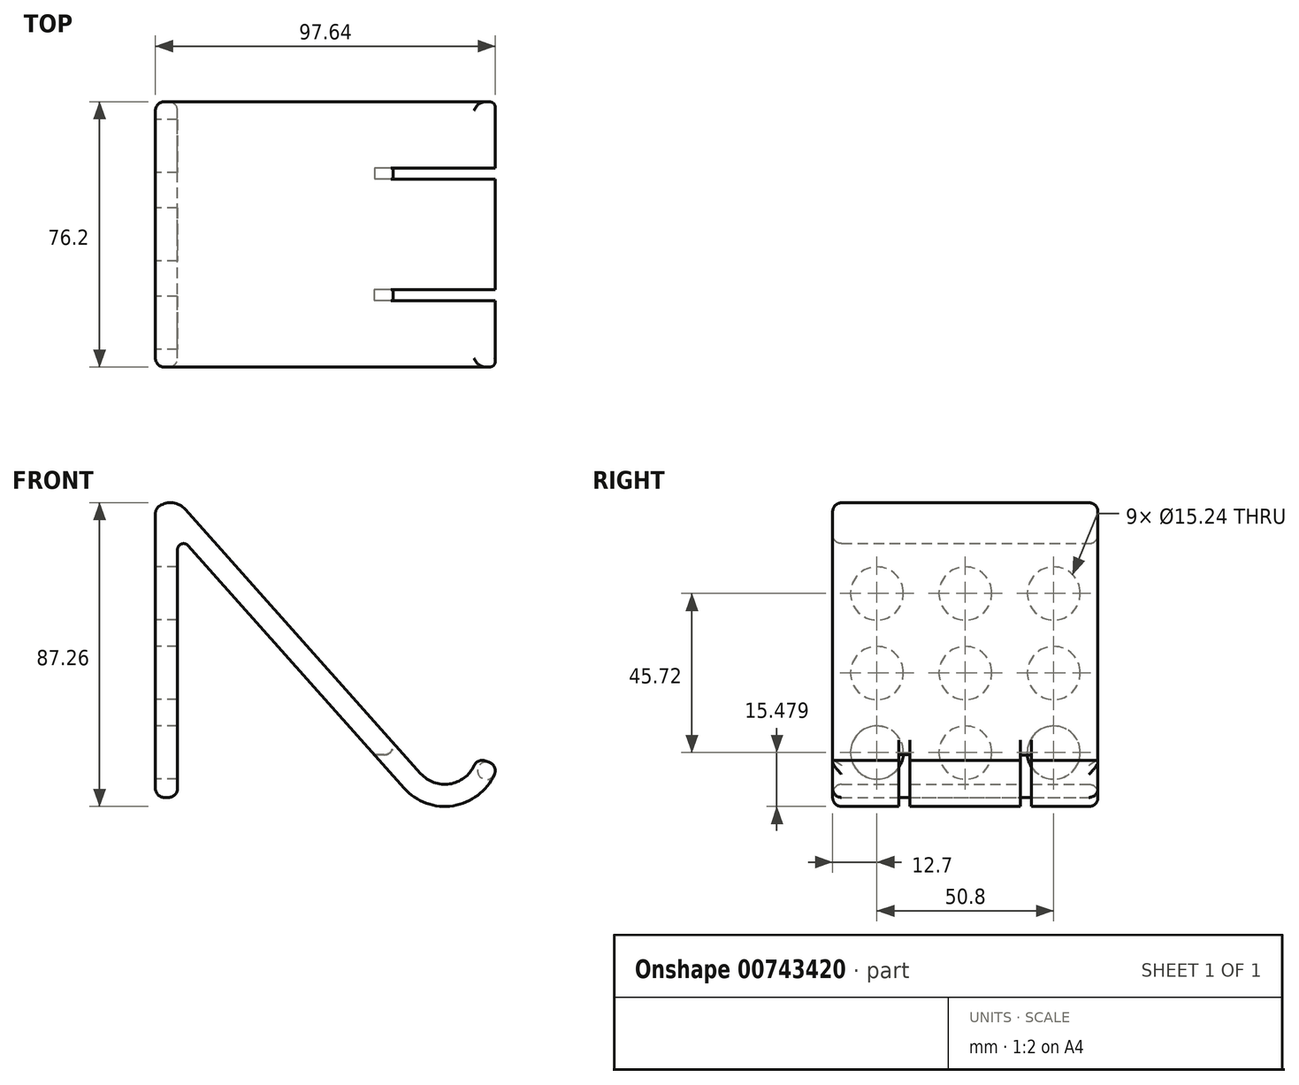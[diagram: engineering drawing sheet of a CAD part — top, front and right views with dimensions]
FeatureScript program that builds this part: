
annotation { "Feature Type Name" : "Feature", "Feature Type Description" : "" }
export const myFeature = defineFeature(function(context is Context, id is Id, definition is map)
    precondition{}
    {
        {
            var Q0;
            Q0=qCreatedBy(makeId("Front.planeOp"),FACE);
            var sketch = newSketch(context, id + "F0", { "sketchPlane" : qUnion([Q0])});
            skLineSegment(sketch, "E0", {"start": v(-38.8, 49.32) * mm, "end": v(28.78, -26.54) * mm});
            skArc(sketch, "E1", {"start": v(28.78, -26.54) * mm, "mid": v(38.21, -29.3) * mm, "end": v(44.82, -22.03) * mm});
            skArc(sketch, "E2", {"start": v(-38.8, 49.32) * mm, "mid": v(-43.13, 51.27) * mm, "end": v(-47.46, 49.32) * mm});
            skLineSegment(sketch, "E3", {"start": v(-47.46, 49.32) * mm, "end": v(-47.46, -33.4) * mm});
            skLineSegment(sketch, "E4", {"start": v(-47.46, -33.4) * mm, "end": v(-41.1, -33.4) * mm});
            skLineSegment(sketch, "E5", {"start": v(-41.1, -33.4) * mm, "end": v(-41.1, 37.8) * mm});
            skLineSegment(sketch, "E6", {"start": v(-38.07, 38.96) * mm, "end": v(24.04, -30.76) * mm});
            skArc(sketch, "E7", {"start": v(24.04, -30.76) * mm, "mid": v(39.43, -35.54) * mm, "end": v(50.85, -24.18) * mm});
            skLineSegment(sketch, "E8", {"start": v(50.85, -24.18) * mm, "end": v(44.82, -22.03) * mm});
            skArc(sketch, "E9", {"start": v(-38.07, 38.96) * mm, "mid": v(-39.99, 39.42) * mm, "end": v(-41.1, 37.8) * mm});
            skSolve(sketch);
        }
        {
            var Q0;
            Q0 = qSketchRegion(id + "F0", true);
            extrude(context, id + "F1", {"entities" : qUnion([Q0]), "depth" : 76.2 * mm, "offsetDistance" : 25.4 * mm});
        }
        {
            var Q0;
            Q0=makeQuery(id+"F1.opExtrude","SWEPT_FACE",FACE,{"disambiguationData":[OSD([sQuery(id+"F0.wireOp",EDGE,"E3")])]});
            var sketch = newSketch(context, id + "F2", { "sketchPlane" : qUnion([Q0])});
            skCircle(sketch, "E10", {"center": v(12.7, -20.51) * mm, "radius": 7.62 * mm});
            skCircle(sketch, "E11.1.0.0", {"center": v(38.1, -20.51) * mm, "radius": 7.62 * mm});
            skCircle(sketch, "E11.2.0.0", {"center": v(63.5, -20.51) * mm, "radius": 7.62 * mm});
            skLineSegment(sketch, "E11.direction1", {"start": v(12.7, -20.51) * mm, "end": v(38.1, -20.51) * mm, "construction": true});
            skCircle(sketch, "E12.1.0.0", {"center": v(12.7, 2.35) * mm, "radius": 7.62 * mm});
            skCircle(sketch, "E12.1.0.1", {"center": v(38.1, 2.35) * mm, "radius": 7.62 * mm});
            skCircle(sketch, "E12.1.0.2", {"center": v(63.5, 2.35) * mm, "radius": 7.62 * mm});
            skCircle(sketch, "E12.2.0.0", {"center": v(12.7, 25.2) * mm, "radius": 7.62 * mm});
            skCircle(sketch, "E12.2.0.1", {"center": v(38.1, 25.2) * mm, "radius": 7.62 * mm});
            skCircle(sketch, "E12.2.0.2", {"center": v(63.5, 25.2) * mm, "radius": 7.62 * mm});
            skLineSegment(sketch, "E12.direction1", {"start": v(12.7, -20.51) * mm, "end": v(12.7, 2.35) * mm, "construction": true});
            skSolve(sketch);
        }
        {
            var Q0;
            Q0 = qSketchRegion(id + "F2", true);
            extrude(context, id + "F3", {"entities" : qUnion([Q0]), "operationType" : NewBodyOperationType.REMOVE, "oppositeDirection" : true, "depth" : 6.35 * mm, "offsetDistance" : 25.4 * mm});
        }
        {
            var Q0;
            Q0=qCreatedBy(makeId("Right.planeOp"),FACE);
            var sketch = newSketch(context, id + "F4", { "sketchPlane" : qUnion([Q0])});
            skLineSegment(sketch, "E13.bottom", {"start": v(-57.15, -21.1) * mm, "end": v(-53.98, -21.1) * mm});
            skLineSegment(sketch, "E13.top", {"start": v(-57.15, -36.34) * mm, "end": v(-53.98, -36.34) * mm});
            skLineSegment(sketch, "E13.left", {"start": v(-57.15, -21.1) * mm, "end": v(-57.15, -36.34) * mm});
            skLineSegment(sketch, "E13.right", {"start": v(-53.98, -21.1) * mm, "end": v(-53.98, -36.34) * mm});
            skLineSegment(sketch, "E14.bottom", {"start": v(-22.23, -21.18) * mm, "end": v(-19.05, -21.18) * mm});
            skLineSegment(sketch, "E14.top", {"start": v(-22.23, -36.42) * mm, "end": v(-19.05, -36.42) * mm});
            skLineSegment(sketch, "E14.left", {"start": v(-22.23, -21.18) * mm, "end": v(-22.23, -36.42) * mm});
            skLineSegment(sketch, "E14.right", {"start": v(-19.05, -21.18) * mm, "end": v(-19.05, -36.42) * mm});
            skSolve(sketch);
        }
        {
            var Q0;
            Q0 = qSketchRegion(id + "F4", true);
            extrude(context, id + "F5", {"entities" : qUnion([Q0]), "operationType" : NewBodyOperationType.REMOVE, "depth" : 76.2 * mm, "offsetDistance" : 25.4 * mm});
        }
        {
            var Q0;
            Q0=makeQuery(id+"F1.opExtrude","SWEPT_EDGE",EDGE,{"disambiguationData":[OSD([sQuery(id+"F0.wireOp",EDGE,"E4"),sQuery(id+"F0.wireOp",EDGE,"E5")])]});
            var Q1;
            Q1=makeQuery(id+"F1.opExtrude","SWEPT_EDGE",EDGE,{"disambiguationData":[OSD([sQuery(id+"F0.wireOp",EDGE,"E3"),sQuery(id+"F0.wireOp",EDGE,"E4")])]});
            var Q2;
            Q2=makeQuery(id+"F1.opExtrude","CAP_EDGE",EDGE,{"disambiguationData":[OSD([sQuery(id+"F0.wireOp",EDGE,"E4")])],"isStart":true});
            var Q3;
            Q3=makeQuery(id+"F1.opExtrude","CAP_EDGE",EDGE,{"disambiguationData":[OSD([sQuery(id+"F0.wireOp",EDGE,"E4")])],"isStart":false});
            var Q4;
            Q4=makeQuery(id+"F1.opExtrude","CAP_EDGE",EDGE,{"disambiguationData":[OSD([sQuery(id+"F0.wireOp",EDGE,"E5")])],"isStart":true});
            var Q5;
            Q5=makeQuery(id+"F1.opExtrude","CAP_EDGE",EDGE,{"disambiguationData":[OSD([sQuery(id+"F0.wireOp",EDGE,"E3")])],"isStart":true});
            var Q6;
            Q6=makeQuery(id+"F1.opExtrude","SWEPT_EDGE",EDGE,{"disambiguationData":[OSD([sQuery(id+"F0.wireOp",EDGE,"E2"),sQuery(id+"F0.wireOp",EDGE,"E3")])]});
            var Q7;
            Q7=makeQuery(id+"F1.opExtrude","CAP_EDGE",EDGE,{"disambiguationData":[OSD([sQuery(id+"F0.wireOp",EDGE,"E3")])],"isStart":false});
            var Q8;
            Q8=makeQuery(id+"F1.opExtrude","CAP_EDGE",EDGE,{"disambiguationData":[OSD([sQuery(id+"F0.wireOp",EDGE,"E5")])],"isStart":false});
            var Q9;
            Q9=makeQuery(id+"F1.opExtrude","CAP_EDGE",EDGE,{"disambiguationData":[OSD([sQuery(id+"F0.wireOp",EDGE,"E2")])],"isStart":true});
            var Q10;
            Q10=makeQuery(id+"F1.opExtrude","CAP_EDGE",EDGE,{"disambiguationData":[OSD([sQuery(id+"F0.wireOp",EDGE,"E0")])],"isStart":true});
            var Q11;
            Q11=makeQuery(id+"F1.opExtrude","CAP_EDGE",EDGE,{"disambiguationData":[OSD([sQuery(id+"F0.wireOp",EDGE,"E2")])],"isStart":false});
            var Q12;
            {var subQ0=sQuery(id+"F0.wireOp",EDGE,"E7");var subQ1=sQuery(id+"F0.wireOp",EDGE,"E8");Q12=makeQuery(id+"F5.boolean.opBoolean","SPLIT",EDGE,{"disambiguationData":[TD([makeQuery(id+"F5.opExtrude","SWEPT_FACE",FACE,{"disambiguationData":[OSD([sQuery(id+"F4.wireOp",EDGE,"E13.right")])]})])],"derivedFrom":makeQuery(id+"F1.opExtrude","SWEPT_EDGE",EDGE,{"disambiguationData":[OSD([subQ0,subQ1])]})});}
            var Q13;
            {var subQ0=sQuery(id+"F0.wireOp",EDGE,"E1");var subQ1=sQuery(id+"F0.wireOp",EDGE,"E8");Q13=makeQuery(id+"F5.boolean.opBoolean","SPLIT",EDGE,{"disambiguationData":[TD([makeQuery(id+"F5.opExtrude","SWEPT_FACE",FACE,{"disambiguationData":[OSD([sQuery(id+"F4.wireOp",EDGE,"E13.right")])]})])],"derivedFrom":makeQuery(id+"F1.opExtrude","SWEPT_EDGE",EDGE,{"disambiguationData":[OSD([subQ0,subQ1])]})});}
            var Q14;
            {var subQ0=sQuery(id+"F0.wireOp",EDGE,"E8");var subQ1=sQuery(id+"F0.wireOp",EDGE,"E7");Q14=makeQuery(id+"F5.boolean.opBoolean","SPLIT",EDGE,{"disambiguationData":[TD([makeQuery(id+"F5.opExtrude","SWEPT_FACE",FACE,{"disambiguationData":[OSD([sQuery(id+"F4.wireOp",EDGE,"E14.right")])]})])],"derivedFrom":makeQuery(id+"F1.opExtrude","SWEPT_EDGE",EDGE,{"disambiguationData":[OSD([subQ1,subQ0])]})});}
            var Q15;
            {var subQ0=sQuery(id+"F0.wireOp",EDGE,"E8");var subQ1=sQuery(id+"F0.wireOp",EDGE,"E1");Q15=makeQuery(id+"F5.boolean.opBoolean","SPLIT",EDGE,{"disambiguationData":[TD([makeQuery(id+"F5.opExtrude","SWEPT_FACE",FACE,{"disambiguationData":[OSD([sQuery(id+"F4.wireOp",EDGE,"E14.right")])]})])],"derivedFrom":makeQuery(id+"F1.opExtrude","SWEPT_EDGE",EDGE,{"disambiguationData":[OSD([subQ1,subQ0])]})});}
            var Q16;
            {var subQ0=sQuery(id+"F0.wireOp",EDGE,"E8");var subQ1=sQuery(id+"F0.wireOp",EDGE,"E7");Q16=makeQuery(id+"F5.boolean.opBoolean","SPLIT",EDGE,{"disambiguationData":[TD([makeQuery(id+"F5.opExtrude","SWEPT_FACE",FACE,{"disambiguationData":[OSD([sQuery(id+"F4.wireOp",EDGE,"E13.left")])]})])],"derivedFrom":makeQuery(id+"F1.opExtrude","SWEPT_EDGE",EDGE,{"disambiguationData":[OSD([subQ1,subQ0])]})});}
            var Q17;
            {var subQ0=sQuery(id+"F0.wireOp",EDGE,"E8");var subQ1=sQuery(id+"F0.wireOp",EDGE,"E1");Q17=makeQuery(id+"F5.boolean.opBoolean","SPLIT",EDGE,{"disambiguationData":[TD([makeQuery(id+"F5.opExtrude","SWEPT_FACE",FACE,{"disambiguationData":[OSD([sQuery(id+"F4.wireOp",EDGE,"E13.left")])]})])],"derivedFrom":makeQuery(id+"F1.opExtrude","SWEPT_EDGE",EDGE,{"disambiguationData":[OSD([subQ1,subQ0])]})});}
            var Q18;
            Q18=makeQuery(id+"F3.boolean.opBoolean","COPY",EDGE,{"derivedFrom":makeQuery(id+"F3.opExtrude","CAP_EDGE",EDGE,{"disambiguationData":[OSD([sQuery(id+"F2.wireOp",EDGE,"E12.1.0.0")])],"isStart":false})});
            var Q19;
            Q19=makeQuery(id+"F3.boolean.opBoolean","COPY",EDGE,{"derivedFrom":makeQuery(id+"F3.opExtrude","CAP_EDGE",EDGE,{"disambiguationData":[OSD([sQuery(id+"F2.wireOp",EDGE,"E12.2.0.0")])],"isStart":false})});
            var Q20;
            Q20=makeQuery(id+"F3.boolean.opBoolean","COPY",EDGE,{"derivedFrom":makeQuery(id+"F3.opExtrude","CAP_EDGE",EDGE,{"disambiguationData":[OSD([sQuery(id+"F2.wireOp",EDGE,"E10")])],"isStart":false})});
            var Q21;
            Q21=makeQuery(id+"F3.boolean.opBoolean","COPY",EDGE,{"derivedFrom":makeQuery(id+"F3.opExtrude","CAP_EDGE",EDGE,{"disambiguationData":[OSD([sQuery(id+"F2.wireOp",EDGE,"E11.1.0.0")])],"isStart":false})});
            var Q22;
            Q22=makeQuery(id+"F3.boolean.opBoolean","COPY",EDGE,{"derivedFrom":makeQuery(id+"F3.opExtrude","CAP_EDGE",EDGE,{"disambiguationData":[OSD([sQuery(id+"F2.wireOp",EDGE,"E12.1.0.1")])],"isStart":false})});
            var Q23;
            Q23=makeQuery(id+"F3.boolean.opBoolean","COPY",EDGE,{"derivedFrom":makeQuery(id+"F3.opExtrude","CAP_EDGE",EDGE,{"disambiguationData":[OSD([sQuery(id+"F2.wireOp",EDGE,"E12.2.0.1")])],"isStart":false})});
            var Q24;
            Q24=makeQuery(id+"F3.boolean.opBoolean","COPY",EDGE,{"derivedFrom":makeQuery(id+"F3.opExtrude","CAP_EDGE",EDGE,{"disambiguationData":[OSD([sQuery(id+"F2.wireOp",EDGE,"E11.2.0.0")])],"isStart":false})});
            var Q25;
            Q25=makeQuery(id+"F3.boolean.opBoolean","COPY",EDGE,{"derivedFrom":makeQuery(id+"F3.opExtrude","CAP_EDGE",EDGE,{"disambiguationData":[OSD([sQuery(id+"F2.wireOp",EDGE,"E12.1.0.2")])],"isStart":false})});
            var Q26;
            Q26=makeQuery(id+"F3.boolean.opBoolean","COPY",EDGE,{"derivedFrom":makeQuery(id+"F3.opExtrude","CAP_EDGE",EDGE,{"disambiguationData":[OSD([sQuery(id+"F2.wireOp",EDGE,"E12.2.0.2")])],"isStart":false})});
            var Q27;
            Q27=makeQuery(id+"F3.boolean.opBoolean","COPY",EDGE,{"derivedFrom":makeQuery(id+"F3.opExtrude","CAP_EDGE",EDGE,{"disambiguationData":[OSD([sQuery(id+"F2.wireOp",EDGE,"E12.2.0.0")])],"isStart":true})});
            var Q28;
            Q28=makeQuery(id+"F3.boolean.opBoolean","COPY",EDGE,{"derivedFrom":makeQuery(id+"F3.opExtrude","CAP_EDGE",EDGE,{"disambiguationData":[OSD([sQuery(id+"F2.wireOp",EDGE,"E12.2.0.1")])],"isStart":true})});
            var Q29;
            Q29=makeQuery(id+"F3.boolean.opBoolean","COPY",EDGE,{"derivedFrom":makeQuery(id+"F3.opExtrude","CAP_EDGE",EDGE,{"disambiguationData":[OSD([sQuery(id+"F2.wireOp",EDGE,"E12.2.0.2")])],"isStart":true})});
            var Q30;
            Q30=makeQuery(id+"F3.boolean.opBoolean","COPY",EDGE,{"derivedFrom":makeQuery(id+"F3.opExtrude","CAP_EDGE",EDGE,{"disambiguationData":[OSD([sQuery(id+"F2.wireOp",EDGE,"E12.1.0.2")])],"isStart":true})});
            var Q31;
            Q31=makeQuery(id+"F3.boolean.opBoolean","COPY",EDGE,{"derivedFrom":makeQuery(id+"F3.opExtrude","CAP_EDGE",EDGE,{"disambiguationData":[OSD([sQuery(id+"F2.wireOp",EDGE,"E12.1.0.1")])],"isStart":true})});
            var Q32;
            Q32=makeQuery(id+"F3.boolean.opBoolean","COPY",EDGE,{"derivedFrom":makeQuery(id+"F3.opExtrude","CAP_EDGE",EDGE,{"disambiguationData":[OSD([sQuery(id+"F2.wireOp",EDGE,"E12.1.0.0")])],"isStart":true})});
            var Q33;
            Q33=makeQuery(id+"F3.boolean.opBoolean","COPY",EDGE,{"derivedFrom":makeQuery(id+"F3.opExtrude","CAP_EDGE",EDGE,{"disambiguationData":[OSD([sQuery(id+"F2.wireOp",EDGE,"E10")])],"isStart":true})});
            var Q34;
            Q34=makeQuery(id+"F3.boolean.opBoolean","COPY",EDGE,{"derivedFrom":makeQuery(id+"F3.opExtrude","CAP_EDGE",EDGE,{"disambiguationData":[OSD([sQuery(id+"F2.wireOp",EDGE,"E11.1.0.0")])],"isStart":true})});
            var Q35;
            Q35=makeQuery(id+"F3.boolean.opBoolean","COPY",EDGE,{"derivedFrom":makeQuery(id+"F3.opExtrude","CAP_EDGE",EDGE,{"disambiguationData":[OSD([sQuery(id+"F2.wireOp",EDGE,"E11.2.0.0")])],"isStart":true})});
            fillet(context, id + "F6", {"entities" : qUnion([Q0, Q1, Q2, Q3, Q4, Q5, Q6, Q7, Q8, Q9, Q10, Q11, Q12, Q13, Q14, Q15, Q16, Q17, Q18, Q19, Q20, Q21, Q22, Q23, Q24, Q25, Q26, Q27, Q28, Q29, Q30, Q31, Q32, Q33, Q34, Q35]), "radius" : 2.54 * mm, "tangentPropagation" : true, "allowEdgeOverflow" : false});
        }
        {
            var Q0;
            Q0=makeQuery(id+"F5.boolean.opBoolean","INTERSECT",EDGE,{"derivedFrom":[makeQuery(id+"F1.opExtrude","SWEPT_FACE",FACE,{"disambiguationData":[OSD([sQuery(id+"F0.wireOp",EDGE,"E0")])]}),makeQuery(id+"F5.opExtrude","SWEPT_FACE",FACE,{"disambiguationData":[OSD([sQuery(id+"F4.wireOp",EDGE,"E13.bottom")])]})]});
            var Q1;
            Q1=makeQuery(id+"F5.boolean.opBoolean","INTERSECT",EDGE,{"derivedFrom":[makeQuery(id+"F1.opExtrude","SWEPT_FACE",FACE,{"disambiguationData":[OSD([sQuery(id+"F0.wireOp",EDGE,"E0")])]}),makeQuery(id+"F5.opExtrude","SWEPT_FACE",FACE,{"disambiguationData":[OSD([sQuery(id+"F4.wireOp",EDGE,"E14.bottom")])]})]});
            fillet(context, id + "F7", {"entities" : qUnion([Q0, Q1]), "radius" : 2.54 * mm, "tangentPropagation" : true, "allowEdgeOverflow" : false});
        }
    });
